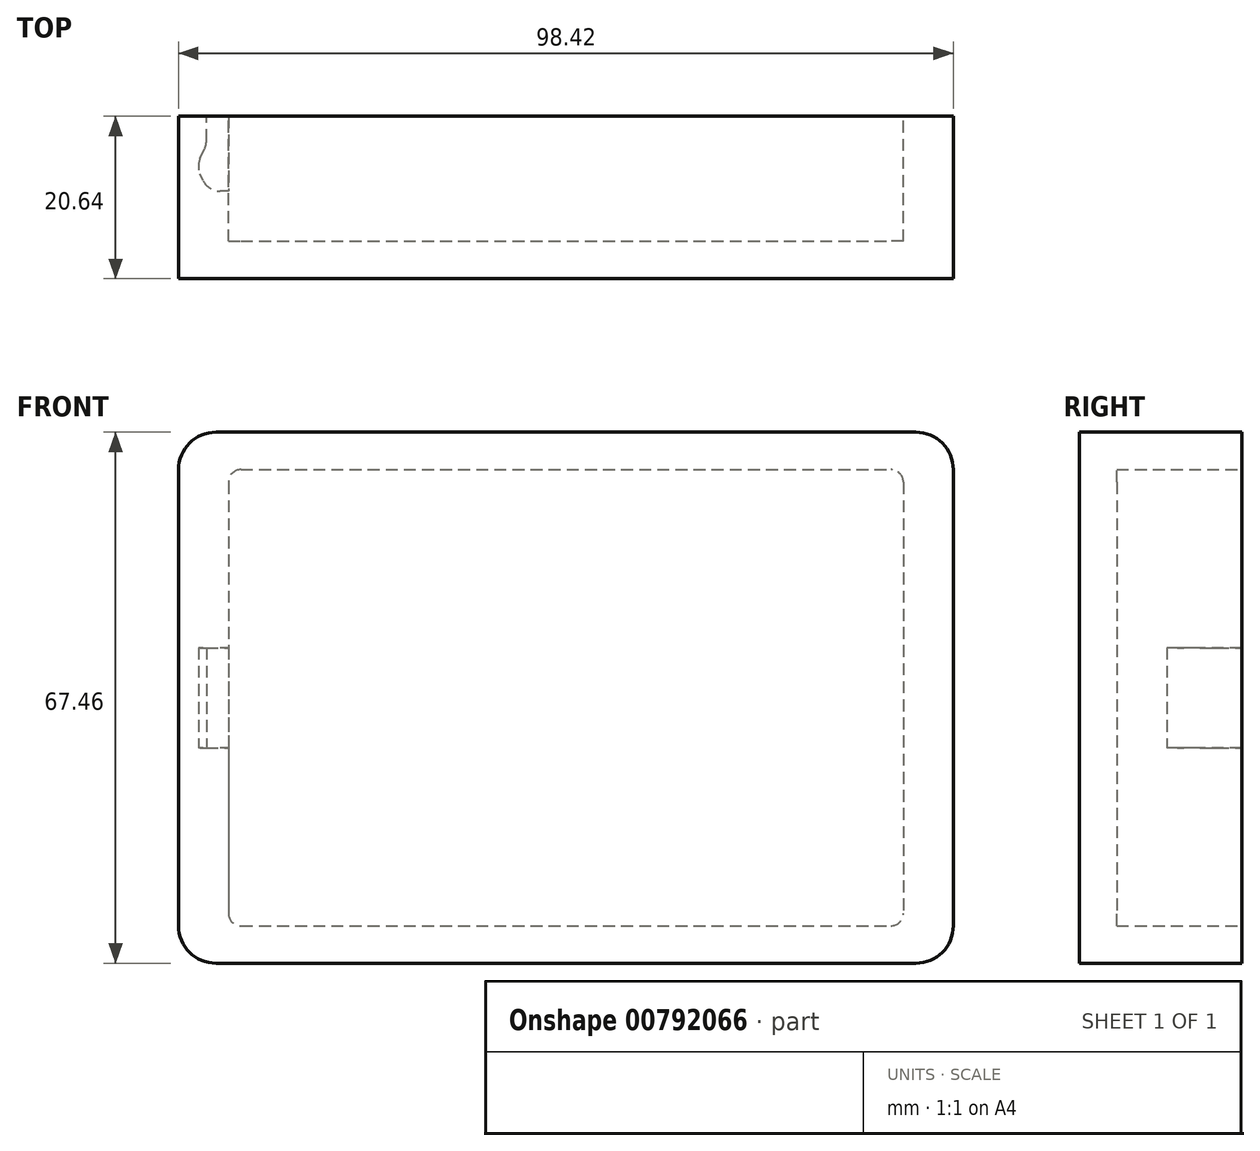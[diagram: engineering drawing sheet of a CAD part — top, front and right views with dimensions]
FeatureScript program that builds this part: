
annotation { "Feature Type Name" : "Feature", "Feature Type Description" : "" }
export const myFeature = defineFeature(function(context is Context, id is Id, definition is map)
    precondition{}
    {
        {
            var Q0;
            Q0=qCreatedBy(makeId("Front.planeOp"),FACE);
            var sketch = newSketch(context, id + "F0", { "sketchPlane" : qUnion([Q0])});
            skLineSegment(sketch, "E0.bottom", {"start": v(-41.28, 28.97) * mm, "end": v(41.28, 28.97) * mm});
            skLineSegment(sketch, "E0.top", {"start": v(-41.28, -28.97) * mm, "end": v(41.28, -28.97) * mm});
            skLineSegment(sketch, "E0.left", {"start": v(-42.86, 27.38) * mm, "end": v(-42.86, -27.38) * mm});
            skLineSegment(sketch, "E0.right", {"start": v(42.86, 27.38) * mm, "end": v(42.86, -27.38) * mm});
            skPoint(sketch, "E0.middle", {"position": v(0, 0) * mm});
            skLineSegment(sketch, "E1.bottom", {"start": v(-44.45, 33.73) * mm, "end": v(44.45, 33.73) * mm});
            skLineSegment(sketch, "E1.top", {"start": v(-44.45, -33.73) * mm, "end": v(44.45, -33.73) * mm});
            skLineSegment(sketch, "E1.left", {"start": v(-49.21, 28.97) * mm, "end": v(-49.21, -28.97) * mm});
            skLineSegment(sketch, "E1.right", {"start": v(49.21, 28.97) * mm, "end": v(49.21, -28.97) * mm});
            skPoint(sketch, "E2.visualSharp", {"position": v(-42.86, 28.97) * mm});
            skArc(sketch, "E2.filletArc", {"start": v(-41.28, 28.97) * mm, "mid": v(-42.4, 28.5) * mm, "end": v(-42.86, 27.38) * mm});
            skPoint(sketch, "E3.visualSharp", {"position": v(42.86, 28.97) * mm});
            skArc(sketch, "E3.filletArc", {"start": v(42.86, 27.38) * mm, "mid": v(42.4, 28.5) * mm, "end": v(41.28, 28.97) * mm});
            skPoint(sketch, "E4.visualSharp", {"position": v(42.86, -28.97) * mm});
            skArc(sketch, "E4.filletArc", {"start": v(41.28, -28.97) * mm, "mid": v(42.4, -28.5) * mm, "end": v(42.86, -27.38) * mm});
            skPoint(sketch, "E5.visualSharp", {"position": v(-42.86, -28.97) * mm});
            skArc(sketch, "E5.filletArc", {"start": v(-42.86, -27.38) * mm, "mid": v(-42.4, -28.5) * mm, "end": v(-41.28, -28.97) * mm});
            skPoint(sketch, "E6.visualSharp", {"position": v(-49.21, -33.73) * mm});
            skArc(sketch, "E6.filletArc", {"start": v(-49.21, -28.97) * mm, "mid": v(-47.82, -32.34) * mm, "end": v(-44.45, -33.73) * mm});
            skPoint(sketch, "E7.visualSharp", {"position": v(-49.21, 33.73) * mm});
            skArc(sketch, "E7.filletArc", {"start": v(-44.45, 33.73) * mm, "mid": v(-47.82, 32.34) * mm, "end": v(-49.21, 28.97) * mm});
            skPoint(sketch, "E8.visualSharp", {"position": v(49.21, 33.73) * mm});
            skArc(sketch, "E8.filletArc", {"start": v(49.21, 28.97) * mm, "mid": v(47.82, 32.34) * mm, "end": v(44.45, 33.73) * mm});
            skPoint(sketch, "E9.visualSharp", {"position": v(49.21, -33.73) * mm});
            skArc(sketch, "E9.filletArc", {"start": v(44.45, -33.73) * mm, "mid": v(47.82, -32.34) * mm, "end": v(49.21, -28.97) * mm});
            skSolve(sketch);
        }
        {
            var Q0;
            Q0=makeQuery(id+"F0.imprint","IMPRINT",FACE,{"disambiguationData":[TD([[makeQuery(id+"F0.imprint","IMPRINT",EDGE,{"derivedFrom":sQuery(id+"F0.wireOp",EDGE,"E0.bottom")}),1.0]])]});
            extrude(context, id + "F1", {"entities" : qUnion([Q0]), "endBound" : BoundingType.SYMMETRIC, "depth" : 15.88 * mm, "offsetDistance" : 25.4 * mm});
        }
        {
            var Q0;
            Q0=makeQuery(id+"F1.opExtrude","CAP_FACE",FACE,{"disambiguationData":[OSD([sQuery(id+"F0.wireOp",EDGE,"E0.bottom"),sQuery(id+"F0.wireOp",EDGE,"E0.top"),sQuery(id+"F0.wireOp",EDGE,"E0.left"),sQuery(id+"F0.wireOp",EDGE,"E0.right"),sQuery(id+"F0.wireOp",EDGE,"E1.bottom"),sQuery(id+"F0.wireOp",EDGE,"E1.top"),sQuery(id+"F0.wireOp",EDGE,"E1.left"),sQuery(id+"F0.wireOp",EDGE,"E1.right"),sQuery(id+"F0.wireOp",EDGE,"E2.filletArc"),sQuery(id+"F0.wireOp",EDGE,"E3.filletArc"),sQuery(id+"F0.wireOp",EDGE,"E4.filletArc"),sQuery(id+"F0.wireOp",EDGE,"E5.filletArc"),sQuery(id+"F0.wireOp",EDGE,"E6.filletArc"),sQuery(id+"F0.wireOp",EDGE,"E7.filletArc"),sQuery(id+"F0.wireOp",EDGE,"E8.filletArc"),sQuery(id+"F0.wireOp",EDGE,"E9.filletArc")])],"isStart":false});
            var sketch = newSketch(context, id + "F2", { "sketchPlane" : qUnion([Q0])});
            skArc(sketch, "E10.0.0", {"start": v(-49.21, -28.97) * mm, "mid": v(-47.82, -32.34) * mm, "end": v(-44.45, -33.73) * mm});
            skLineSegment(sketch, "E10.0.1", {"start": v(-44.45, -33.73) * mm, "end": v(44.45, -33.73) * mm});
            skArc(sketch, "E10.0.2", {"start": v(44.45, -33.73) * mm, "mid": v(47.82, -32.34) * mm, "end": v(49.21, -28.97) * mm});
            skLineSegment(sketch, "E10.0.3", {"start": v(49.21, -28.97) * mm, "end": v(49.21, 28.97) * mm});
            skArc(sketch, "E10.0.4", {"start": v(49.21, 28.97) * mm, "mid": v(47.82, 32.34) * mm, "end": v(44.45, 33.73) * mm});
            skLineSegment(sketch, "E10.0.5", {"start": v(44.45, 33.73) * mm, "end": v(-44.45, 33.73) * mm});
            skArc(sketch, "E10.0.6", {"start": v(-44.45, 33.73) * mm, "mid": v(-47.82, 32.34) * mm, "end": v(-49.21, 28.97) * mm});
            skLineSegment(sketch, "E10.0.7", {"start": v(-49.21, 28.97) * mm, "end": v(-49.21, -28.97) * mm});
            skSolve(sketch);
        }
        {
            var Q0;
            Q0=makeQuery(id+"F2.imprint","IMPRINT",FACE,{"disambiguationData":[TD([[makeQuery(id+"F2.imprint","IMPRINT",EDGE,{"derivedFrom":sQuery(id+"F2.wireOp",EDGE,"E10.0.0")}),1.0]])]});
            var Q1;
            Q1=makeQuery(id+"F2.imprint","IMPRINT",FACE,{"disambiguationData":[TD([[makeQuery(id+"F2.imprint","IMPRINT",EDGE,{"derivedFrom":makeQuery(id+"F1.opExtrude","CAP_EDGE",EDGE,{"disambiguationData":[OSD([sQuery(id+"F0.wireOp",EDGE,"E0.bottom")])],"isStart":false})}),-1.0]])]});
            extrude(context, id + "F3", {"entities" : qUnion([Q0, Q1]), "operationType" : NewBodyOperationType.ADD, "depth" : 4.76 * mm, "offsetDistance" : 25.4 * mm});
        }
        {
            var Q0;
            Q0=qCreatedBy(makeId("Top.planeOp"),FACE);
            var sketch = newSketch(context, id + "F4", { "sketchPlane" : qUnion([Q0])});
            skLineSegment(sketch, "E11.0", {"start": v(-42.86, -7.94) * mm, "end": v(-42.86, 7.94) * mm, "construction": true});
            skLineSegment(sketch, "E12.0", {"start": v(42.86, -7.94) * mm, "end": v(42.86, 7.94) * mm});
            skPoint(sketch, "E13.visualSharp", {"position": v(-46.06, 2.72) * mm});
            skLineSegment(sketch, "E14", {"start": v(-42.86, -1.59) * mm, "end": v(-43.92, -1.59) * mm});
            skLineSegment(sketch, "E15", {"start": v(-46.08, -0.21) * mm, "end": v(-46.45, 0.58) * mm});
            skLineSegment(sketch, "E16", {"start": v(-46.45, 2.6) * mm, "end": v(-45.88, 3.82) * mm});
            skLineSegment(sketch, "E17", {"start": v(-45.66, 4.82) * mm, "end": v(-45.66, 7.94) * mm});
            skLineSegment(sketch, "E18", {"start": v(-45.66, 7.94) * mm, "end": v(-42.86, 7.94) * mm});
            skLineSegment(sketch, "E19", {"start": v(-42.86, 7.94) * mm, "end": v(-42.86, -1.59) * mm});
            skPoint(sketch, "E20.visualSharp", {"position": v(-46.92, 1.59) * mm});
            skArc(sketch, "E20.filletArc", {"start": v(-46.45, 2.6) * mm, "mid": v(-46.67, 1.59) * mm, "end": v(-46.45, 0.58) * mm});
            skPoint(sketch, "E21.visualSharp", {"position": v(-45.66, 4.3) * mm});
            skArc(sketch, "E21.filletArc", {"start": v(-45.88, 3.82) * mm, "mid": v(-45.71, 4.3) * mm, "end": v(-45.66, 4.82) * mm});
            skArc(sketch, "E22.filletArc", {"start": v(-46.08, -0.21) * mm, "mid": v(-45.2, -1.21) * mm, "end": v(-43.92, -1.59) * mm});
            skLineSegment(sketch, "E23", {"start": v(-44.3, 1.59) * mm, "end": v(-42.86, 1.59) * mm});
            skSolve(sketch);
        }
        {
            var Q0;
            {var subQ0=sQuery(id+"F4.wireOp",EDGE,"E14");Q0=makeQuery(id+"F4.imprint","IMPRINT",FACE,{"disambiguationData":[TD([[makeQuery(id+"F4.imprint","IMPRINT",EDGE,{"derivedFrom":subQ0}),-1.0]])]});}
            extrude(context, id + "F5", {"entities" : qUnion([Q0]), "operationType" : NewBodyOperationType.REMOVE, "endBound" : BoundingType.SYMMETRIC, "depth" : 12.7 * mm, "offsetDistance" : 25.4 * mm});
        }
    });
